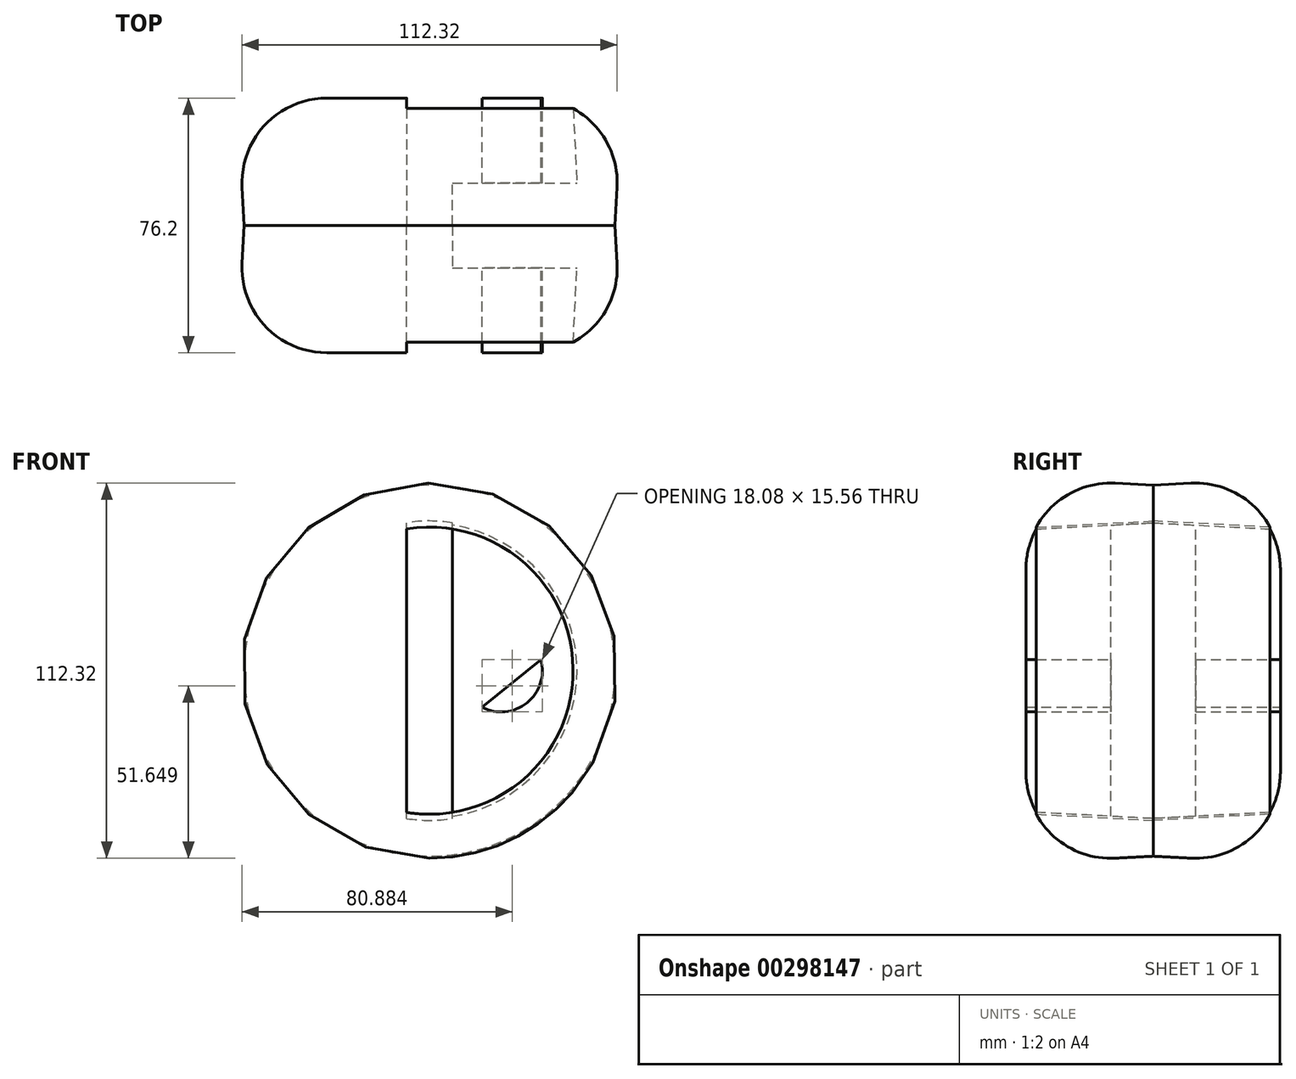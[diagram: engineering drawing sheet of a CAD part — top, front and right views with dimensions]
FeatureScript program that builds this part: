
annotation { "Feature Type Name" : "Feature", "Feature Type Description" : "" }
export const myFeature = defineFeature(function(context is Context, id is Id, definition is map)
    precondition{}
    {
        {
            var Q0;
            Q0=qCreatedBy(makeId("Front.planeOp"),FACE);
            var sketch = newSketch(context, id + "F0", { "sketchPlane" : qUnion([Q0])});
            skCircle(sketch, "E0", {"center": v(0, 0) * mm, "radius": 55.53 * mm});
            skCircle(sketch, "E1", {"center": v(0, 0) * mm, "radius": 44.8 * mm});
            skLineSegment(sketch, "E2.bottom", {"start": v(6.86, -46.44) * mm, "end": v(-6.86, -46.44) * mm});
            skLineSegment(sketch, "E2.top", {"start": v(6.86, 48.64) * mm, "end": v(-6.86, 48.64) * mm});
            skLineSegment(sketch, "E2.left", {"start": v(6.86, -46.44) * mm, "end": v(6.86, 48.64) * mm});
            skLineSegment(sketch, "E2.right", {"start": v(-6.86, -46.44) * mm, "end": v(-6.86, 48.64) * mm});
            skArc(sketch, "E3", {"start": v(-33.33, 3.27) * mm, "mid": v(-29.16, -9.62) * mm, "end": v(-15.68, -10.94) * mm});
            skLineSegment(sketch, "E4", {"start": v(-33.33, 3.27) * mm, "end": v(-15.68, -10.94) * mm});
            skLineSegment(sketch, "E5.MirrorCS", {"start": v(33.33, 3.27) * mm, "end": v(15.68, -10.94) * mm});
            skArc(sketch, "E6.MirrorCS", {"start": v(33.33, 3.27) * mm, "mid": v(29.16, -9.62) * mm, "end": v(15.68, -10.94) * mm});
            skSolve(sketch);
        }
        {
            var Q0;
            Q0=makeQuery(id+"F0.imprint","IMPRINT",FACE,{"disambiguationData":[TD([[makeQuery(id+"F0.imprint","IMPRINT",EDGE,{"derivedFrom":sQuery(id+"F0.wireOp",EDGE,"E0")}),1.0]])]});
            var Q1;
            {var subQ5=sQuery(id+"F0.wireOp",EDGE,"E2.top");Q1=makeQuery(id+"F0.imprint","IMPRINT",FACE,{"disambiguationData":[TD([[makeQuery(id+"F0.imprint","IMPRINT",EDGE,{"derivedFrom":subQ5}),1.0]])]});}
            var Q2;
            {var subQ5=sQuery(id+"F0.wireOp",EDGE,"E2.bottom");Q2=makeQuery(id+"F0.imprint","IMPRINT",FACE,{"disambiguationData":[TD([[makeQuery(id+"F0.imprint","IMPRINT",EDGE,{"derivedFrom":subQ5}),-1.0]])]});}
            extrude(context, id + "F1", {"entities" : qUnion([Q0, Q1, Q2]), "endBound" : BoundingType.SYMMETRIC, "depth" : 76.2 * mm, "hasDraft" : true, "draftAngle" : 3 * degree});
        }
        {
            var Q0;
            {var subQ0=sQuery(id+"F0.wireOp",EDGE,"E2.right");var subQ1=sQuery(id+"F0.wireOp",EDGE,"E1");var subQ2=makeQuery(id+"F0.imprint","INTERSECT",VERTEX,{"disambiguationData":[OD(0.0)],"derivedFrom":[subQ1,subQ0]});Q0=makeQuery(id+"F0.imprint","IMPRINT",FACE,{"disambiguationData":[TD([[makeQuery(id+"F0.imprint","IMPRINT",EDGE,{"disambiguationData":[TD([[subQ2,1.0]])],"derivedFrom":subQ1}),1.0]])]});}
            extrude(context, id + "F2", {"entities" : qUnion([Q0]), "operationType" : NewBodyOperationType.ADD, "endBound" : BoundingType.SYMMETRIC, "depth" : 76.2 * mm});
        }
        {
            var Q0;
            Q0=makeQuery(id+"F0.imprint","IMPRINT",FACE,{"disambiguationData":[TD([[makeQuery(id+"F0.imprint","IMPRINT",EDGE,{"derivedFrom":sQuery(id+"F0.wireOp",EDGE,"E3")}),-1.0]])]});
            var Q1;
            Q1=makeQuery(id+"F0.imprint","IMPRINT",FACE,{"disambiguationData":[TD([[makeQuery(id+"F0.imprint","IMPRINT",EDGE,{"derivedFrom":sQuery(id+"F0.wireOp",EDGE,"E5.MirrorCS")}),-1.0]])]});
            extrude(context, id + "F3", {"entities" : qUnion([Q0, Q1]), "operationType" : NewBodyOperationType.ADD, "endBound" : BoundingType.SYMMETRIC, "depth" : 25.4 * mm});
        }
        {
            var Q0;
            Q0=makeQuery(id+"F0.imprint","IMPRINT",FACE,{"disambiguationData":[TD([[makeQuery(id+"F0.imprint","IMPRINT",EDGE,{"derivedFrom":sQuery(id+"F0.wireOp",EDGE,"E3")}),1.0]])]});
            var Q1;
            Q1=makeQuery(id+"F0.imprint","IMPRINT",FACE,{"disambiguationData":[TD([[makeQuery(id+"F0.imprint","IMPRINT",EDGE,{"derivedFrom":sQuery(id+"F0.wireOp",EDGE,"E5.MirrorCS")}),1.0]])]});
            extrude(context, id + "F4", {"entities" : qUnion([Q0, Q1]), "operationType" : NewBodyOperationType.ADD, "endBound" : BoundingType.SYMMETRIC, "depth" : 76.2 * mm});
        }
        {
            var Q0;
            Q0=makeQuery(id+"F1.opExtrude","CAP_EDGE",EDGE,{"disambiguationData":[OSD([sQuery(id+"F0.wireOp",EDGE,"E0")])],"isStart":false});
            fillet(context, id + "F5", {"entities" : qUnion([Q0]), "radius" : 25.4 * mm, "tangentPropagation" : true, "allowEdgeOverflow" : false});
        }
        {
            var Q0;
            Q0=makeQuery(id+"F1.opExtrude","CAP_EDGE",EDGE,{"disambiguationData":[OSD([sQuery(id+"F0.wireOp",EDGE,"E0")])],"isStart":true});
            fillet(context, id + "F6", {"entities" : qUnion([Q0]), "radius" : 25.4 * mm, "tangentPropagation" : true, "allowEdgeOverflow" : false});
        }
    });
